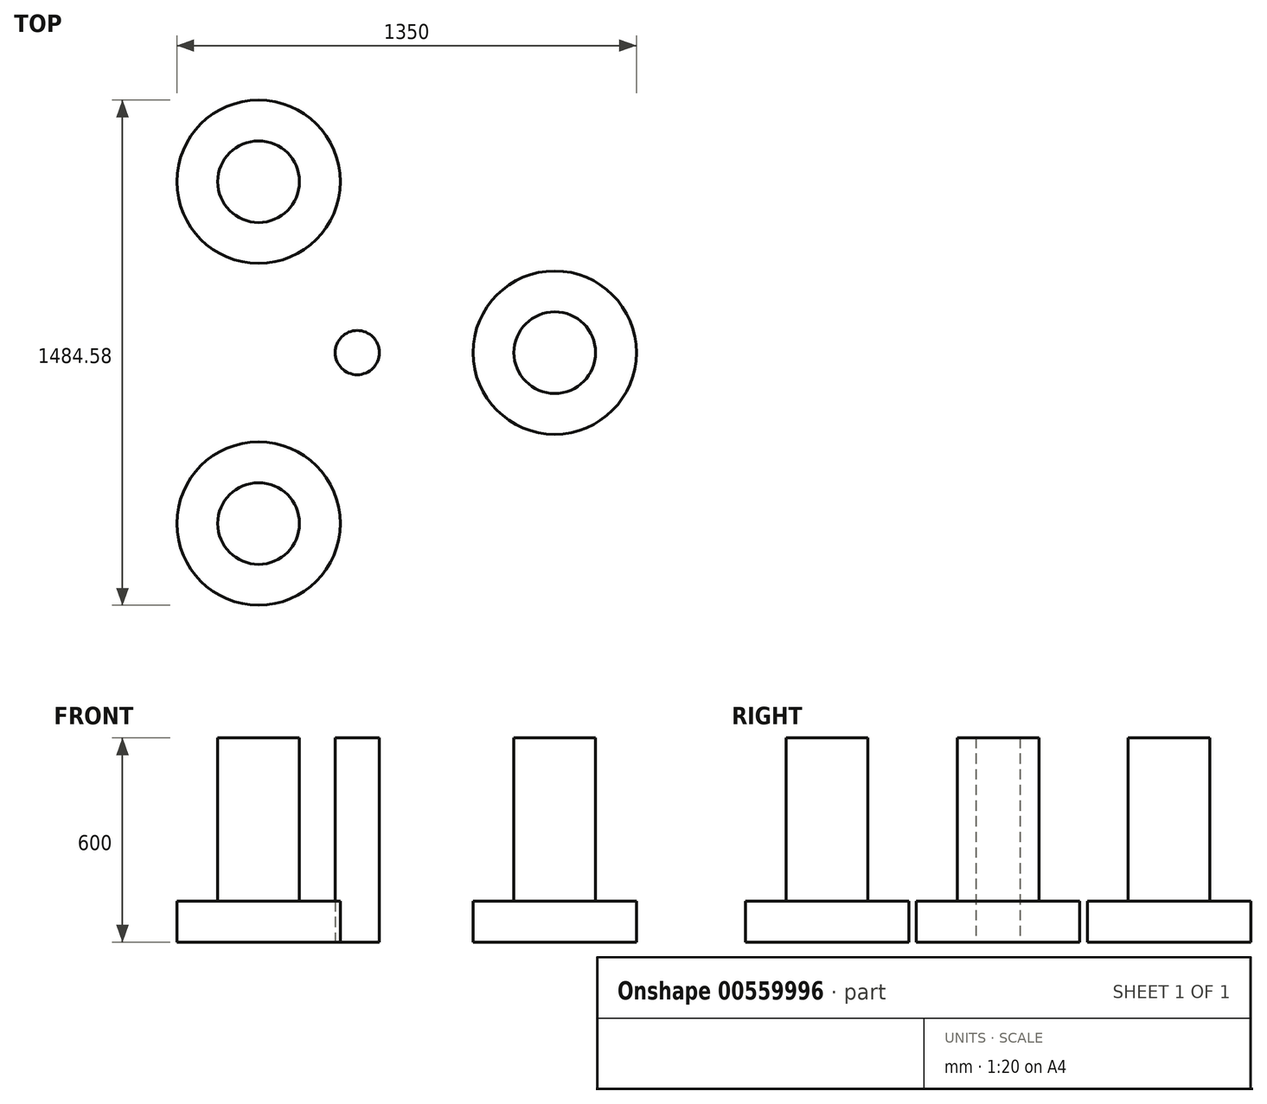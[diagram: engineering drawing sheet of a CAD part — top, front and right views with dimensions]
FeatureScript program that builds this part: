
annotation { "Feature Type Name" : "Feature", "Feature Type Description" : "" }
export const myFeature = defineFeature(function(context is Context, id is Id, definition is map)
    precondition{}
    {
        {
            var Q0;
            Q0=qCreatedBy(makeId("Top.planeOp"),FACE);
            var sketch = newSketch(context, id + "F0", { "sketchPlane" : qUnion([Q0])});
            skCircle(sketch, "E0", {"center": v(0, 0) * mm, "radius": 3250 * mm});
            skSolve(sketch);
        }
        {
            var Q0;
            Q0=makeQuery(id+"F0.imprint","IMPRINT",FACE,{"disambiguationData":[TD([[makeQuery(id+"F0.imprint","IMPRINT",EDGE,{"derivedFrom":sQuery(id+"F0.wireOp",EDGE,"E0")}),1.0]])]});
            extrude(context, id + "F1", {"entities" : qUnion([Q0]), "depth" : 30000 * mm, "offsetDistance" : 25.4 * mm});
        }
        {
            var Q0;
            Q0=qCreatedBy(makeId("Top.planeOp"),FACE);
            var sketch = newSketch(context, id + "F2", { "sketchPlane" : qUnion([Q0])});
            skCircle(sketch, "E1", {"center": v(29000, 0) * mm, "radius": 12000 * mm});
            skSolve(sketch);
        }
        {
            var Q0;
            Q0=makeQuery(id+"F2.imprint","IMPRINT",FACE,{"disambiguationData":[TD([[makeQuery(id+"F2.imprint","IMPRINT",EDGE,{"derivedFrom":sQuery(id+"F2.wireOp",EDGE,"E1")}),1.0]])]});
            extrude(context, id + "F3", {"entities" : qUnion([Q0]), "depth" : 6000 * mm, "offsetDistance" : 25.4 * mm});
        }
        {
            var Q0;
            Q0=makeQuery(id+"F3.opExtrude","CAP_FACE",FACE,{"disambiguationData":[OSD([sQuery(id+"F2.wireOp",EDGE,"E1")])],"isStart":false});
            var sketch = newSketch(context, id + "F4", { "sketchPlane" : qUnion([Q0])});
            skCircle(sketch, "E2", {"center": v(29000, 0) * mm, "radius": 6000 * mm});
            skSolve(sketch);
        }
        {
            var Q0;
            Q0=makeQuery(id+"F4.imprint","IMPRINT",FACE,{"disambiguationData":[TD([[makeQuery(id+"F4.imprint","IMPRINT",EDGE,{"derivedFrom":sQuery(id+"F4.wireOp",EDGE,"E2")}),1.0]])]});
            extrude(context, id + "F5", {"entities" : qUnion([Q0]), "operationType" : NewBodyOperationType.ADD, "depth" : 24000 * mm, "offsetDistance" : 25.4 * mm});
        }
        {
            var Q0;
            Q0=makeQuery(id+"F3.opExtrude","SWEPT_BODY",BODY,{"disambiguationData":[OSD([sQuery(id+"F2.wireOp",EDGE,"E1")])]});
            var Q1;
            Q1=makeQuery(id+"F1.opExtrude","SWEPT_BODY",BODY,{"disambiguationData":[OSD([sQuery(id+"F0.wireOp",EDGE,"E0")])]});
            var Q2;
            Q2=makeQuery(id+"F1.opExtrude","SWEPT_FACE",FACE,{"disambiguationData":[OSD([sQuery(id+"F0.wireOp",EDGE,"E0")])]});
            circularPattern(context, id + "F6", {"entities" : qUnion([Q0, Q1]), "axis" : qUnion([Q2]), "angle" : 360 * degree, "instanceCount" : 3, "equalSpace" : true});
        }
        {
            var Q0;
            Q0=makeQuery(id+"F1.opExtrude","SWEPT_BODY",BODY,{"disambiguationData":[OSD([sQuery(id+"F0.wireOp",EDGE,"E0")])]});
            var Q1;
            Q1=makeQuery(id+"F3.opExtrude","SWEPT_BODY",BODY,{"disambiguationData":[OSD([sQuery(id+"F2.wireOp",EDGE,"E1")])]});
            var Q2;
            Q2=makeQuery(id+"F6.opPattern","COPY",BODY,{"derivedFrom":makeQuery(id+"F3.opExtrude","SWEPT_BODY",BODY,{"disambiguationData":[OSD([sQuery(id+"F2.wireOp",EDGE,"E1")])]}),"instanceName":"1"});
            var Q3;
            Q3=makeQuery(id+"F6.opPattern","COPY",BODY,{"derivedFrom":makeQuery(id+"F3.opExtrude","SWEPT_BODY",BODY,{"disambiguationData":[OSD([sQuery(id+"F2.wireOp",EDGE,"E1")])]}),"instanceName":"2"});
            var Q4;
            Q4=makeQuery(id+"F6.opPattern","COPY",BODY,{"derivedFrom":makeQuery(id+"F1.opExtrude","SWEPT_BODY",BODY,{"disambiguationData":[OSD([sQuery(id+"F0.wireOp",EDGE,"E0")])]}),"instanceName":"2"});
            var Q5;
            Q5=makeQuery(id+"F6.opPattern","COPY",BODY,{"derivedFrom":makeQuery(id+"F1.opExtrude","SWEPT_BODY",BODY,{"disambiguationData":[OSD([sQuery(id+"F0.wireOp",EDGE,"E0")])]}),"instanceName":"1"});
            var Q6;
            Q6=qCreatedBy(makeId("Origin.pointOp"),VERTEX);
            transform(context, id + "F7", {"entities" : qUnion([Q0, Q1, Q2, Q3, Q4, Q5]), "transformType" : TransformType.SCALE_UNIFORMLY, "scale" : 0.02, "scalePoint" : qUnion([Q6]), "makeCopy" : false});
        }
    });
